# Revit family: Counter_Top-Vanity_Top-KOHLER-Solid_Expressions-K-5441
name_source: partatom
category: Casework
revit_build: Autodesk Revit 2015 (Build: 20140606_1530(x64)
units: mm (PartAtom-declared; Revit-internal decimal feet)

## types (4) — shared parameters
ADA Compliant = No
Assembly Code = E2010
Construction Type = ITB
Date Modified = 11/02/2018
Default Elevation = 0"
Depth = 22 13/16"
Description = 61 Inch vanity top without cutout
Hardware Included = No
Height = 1"
Manufacturer = KOHLER Co.
MasterFormat 1995 = 08715
MasterFormat 2004 = 08.71.73
Material = Solid Surface
Product Documentation Link = http://www.us.kohler.com
Product Name = Solid/Expressions
Product Page URL = http://www.us.kohler.com
URL = https://www.us.kohler.com
Width = 61"

## per-type parameters (varying)
| type | Finish | Model | Product Finish | Type |
| S33-White Expressions | Kohler-Solid_Surface-S33-White_Expressions | K-5441-S33 | Kohler-Solid_Surface-S33-White_Expressions | 1 |
| S34-Almond Expressions | Kohler-Solid_Surface-S34-Almond_Expressions | K-5441-S34 | Kohler-Solid_Surface-S34-Almond_Expressions | 2 |
| S35-Biscuit Expressions | Kohler-Solid_Surface-S35-Biscuit_Expressions | K-5441-S35 | Kohler-Solid_Surface-S35-Biscuit_Expressions | 3 |
| S36-Ice Grey Expressions | Kohler-Solid_Surface-S36-Ice_Grey_Expressions | K-5441-S36 | Kohler-Solid_Surface-S36-Ice_Grey_Expressions | 4 |

## geometry (parser evidence)
native form markers: Sweep x6
no freeform markers — native parametric forms only
